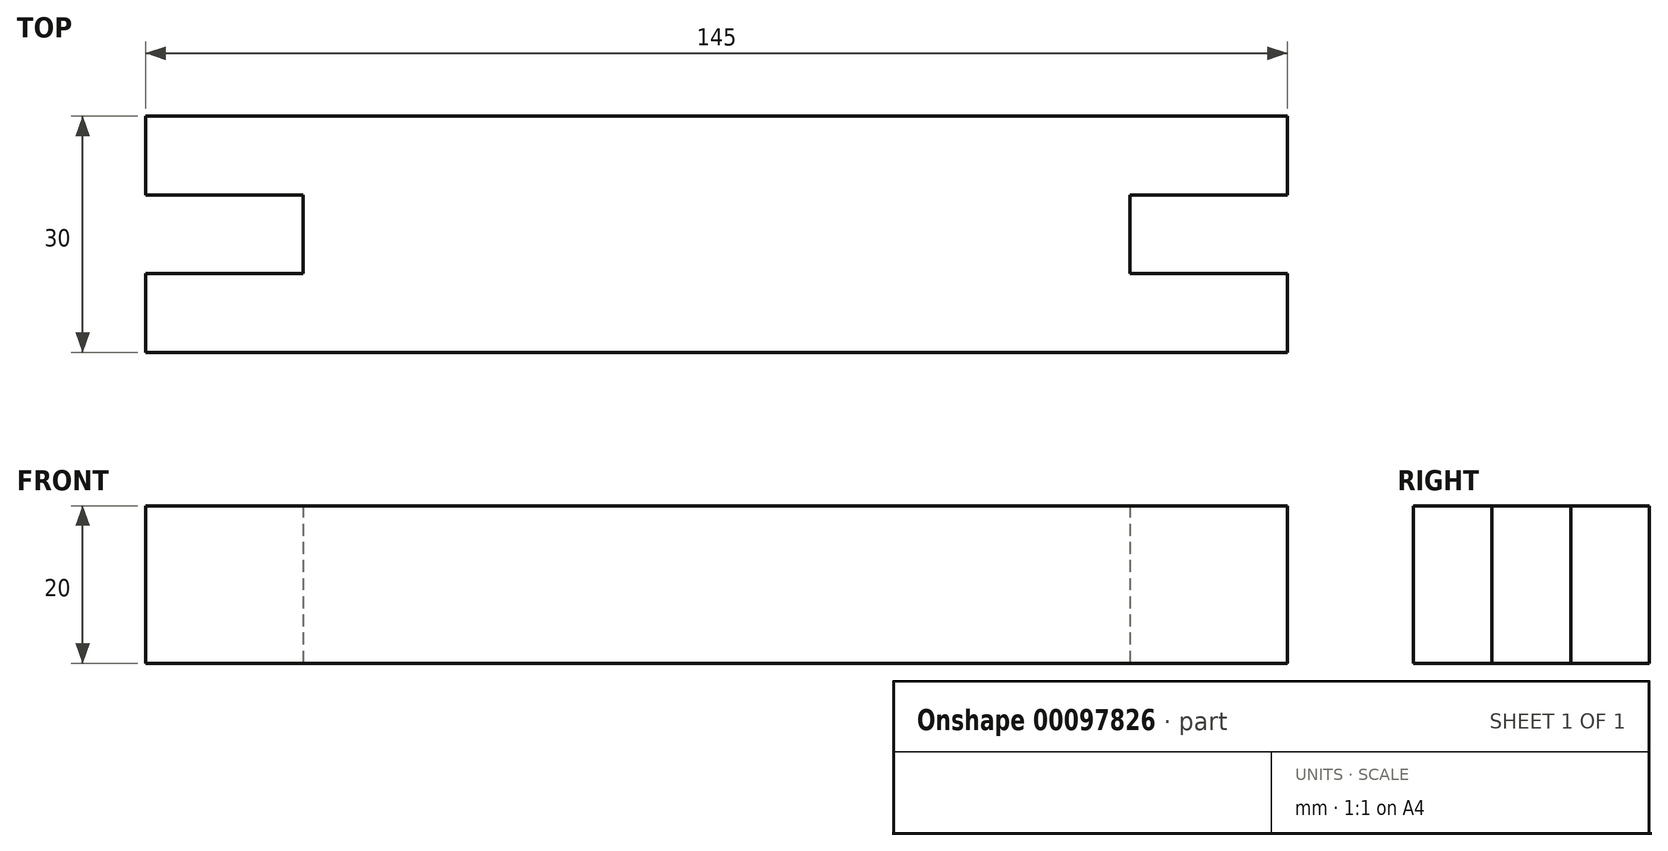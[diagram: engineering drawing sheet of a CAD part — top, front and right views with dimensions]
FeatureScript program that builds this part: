
annotation { "Feature Type Name" : "Feature", "Feature Type Description" : "" }
export const myFeature = defineFeature(function(context is Context, id is Id, definition is map)
    precondition{}
    {
        {
            var Q0;
            Q0=qCreatedBy(makeId("Top.planeOp"),FACE);
            var sketch = newSketch(context, id + "F0", { "sketchPlane" : qUnion([Q0])});
            skLineSegment(sketch, "E0.bottom", {"start": v(72.5, 15) * mm, "end": v(-72.5, 15) * mm});
            skLineSegment(sketch, "E0.top", {"start": v(72.5, -15) * mm, "end": v(-72.5, -15) * mm});
            skLineSegment(sketch, "E0.left", {"start": v(72.5, 15) * mm, "end": v(72.5, 5) * mm});
            skLineSegment(sketch, "E0.right", {"start": v(-72.5, 15) * mm, "end": v(-72.5, 5) * mm});
            skPoint(sketch, "E0.middle", {"position": v(0, 0) * mm});
            skLineSegment(sketch, "E1.bottom", {"start": v(-52.5, -5) * mm, "end": v(-72.5, -5) * mm});
            skLineSegment(sketch, "E1.top", {"start": v(-52.5, 5) * mm, "end": v(-72.5, 5) * mm});
            skLineSegment(sketch, "E1.left", {"start": v(-52.5, -5) * mm, "end": v(-52.5, 5) * mm});
            skPoint(sketch, "E1.middle", {"position": v(-72.5, 0) * mm});
            skLineSegment(sketch, "E2.MirrorCS", {"start": v(52.5, 5) * mm, "end": v(72.5, 5) * mm});
            skLineSegment(sketch, "E3.MirrorCS", {"start": v(52.5, -5) * mm, "end": v(52.5, 5) * mm});
            skLineSegment(sketch, "E4.MirrorCS", {"start": v(52.5, -5) * mm, "end": v(72.5, -5) * mm});
            skLineSegment(sketch, "E5.trimOffspring", {"start": v(-72.5, -5) * mm, "end": v(-72.5, -15) * mm});
            skPoint(sketch, "E1.right.end.orphan", {"position": v(-92.5, 5) * mm});
            skPoint(sketch, "E1.right.start.orphan", {"position": v(-92.5, -5) * mm});
            skLineSegment(sketch, "E6.trimOffspring", {"start": v(72.5, -5) * mm, "end": v(72.5, -15) * mm});
            skPoint(sketch, "E7.orphan", {"position": v(92.5, 5) * mm});
            skPoint(sketch, "E8.orphan", {"position": v(92.5, -5) * mm});
            skSolve(sketch);
        }
        {
            var Q0;
            Q0=makeQuery(id+"F0.imprint","IMPRINT",FACE,{"disambiguationData":[TD([[makeQuery(id+"F0.imprint","IMPRINT",EDGE,{"derivedFrom":sQuery(id+"F0.wireOp",EDGE,"E0.bottom")}),1.0]])]});
            extrude(context, id + "F1", {"entities" : qUnion([Q0]), "depth" : 20 * mm});
        }
    });
